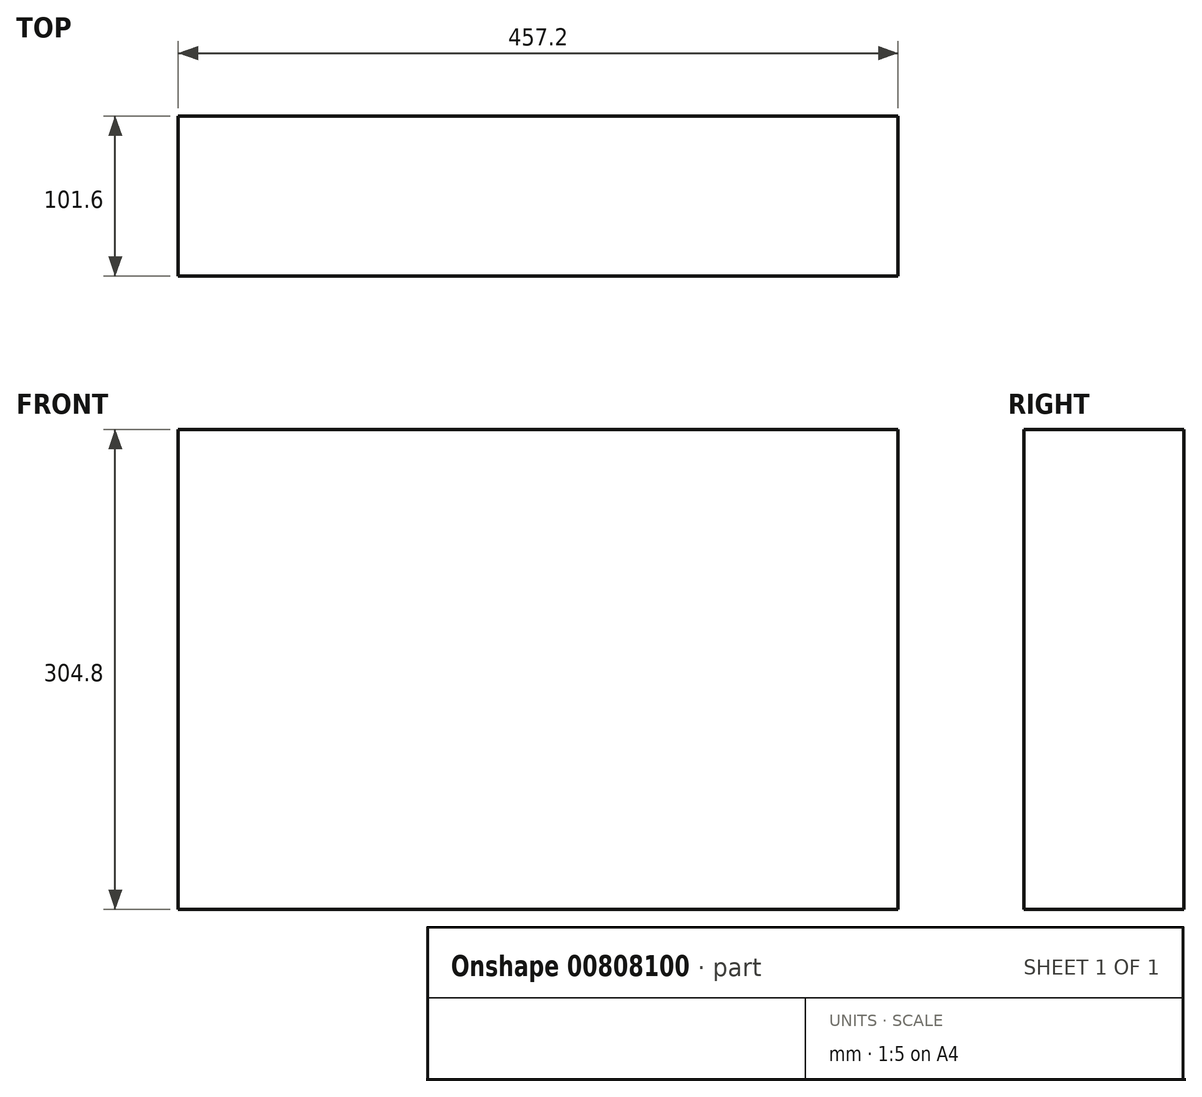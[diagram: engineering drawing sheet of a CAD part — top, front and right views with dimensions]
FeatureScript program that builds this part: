
annotation { "Feature Type Name" : "Feature", "Feature Type Description" : "" }
export const myFeature = defineFeature(function(context is Context, id is Id, definition is map)
    precondition{}
    {
        {
            var Q0;
            Q0=qCreatedBy(makeId("Front.planeOp"),FACE);
            var sketch = newSketch(context, id + "F0", { "sketchPlane" : qUnion([Q0])});
            skLineSegment(sketch, "E0.bottom", {"start": v(228.6, 152.4) * mm, "end": v(-228.6, 152.4) * mm});
            skLineSegment(sketch, "E0.top", {"start": v(228.6, -152.4) * mm, "end": v(-228.6, -152.4) * mm});
            skLineSegment(sketch, "E0.left", {"start": v(228.6, 152.4) * mm, "end": v(228.6, -152.4) * mm});
            skLineSegment(sketch, "E0.right", {"start": v(-228.6, 152.4) * mm, "end": v(-228.6, -152.4) * mm});
            skPoint(sketch, "E0.middle", {"position": v(0, 0) * mm});
            skSolve(sketch);
        }
        {
            var Q0;
            Q0=qSketchRegion(id+"F0",true);
            extrude(context, id + "F1", {"entities" : qUnion([Q0]), "depth" : 101.6 * mm, "offsetDistance" : 25.4 * mm});
        }
    });
